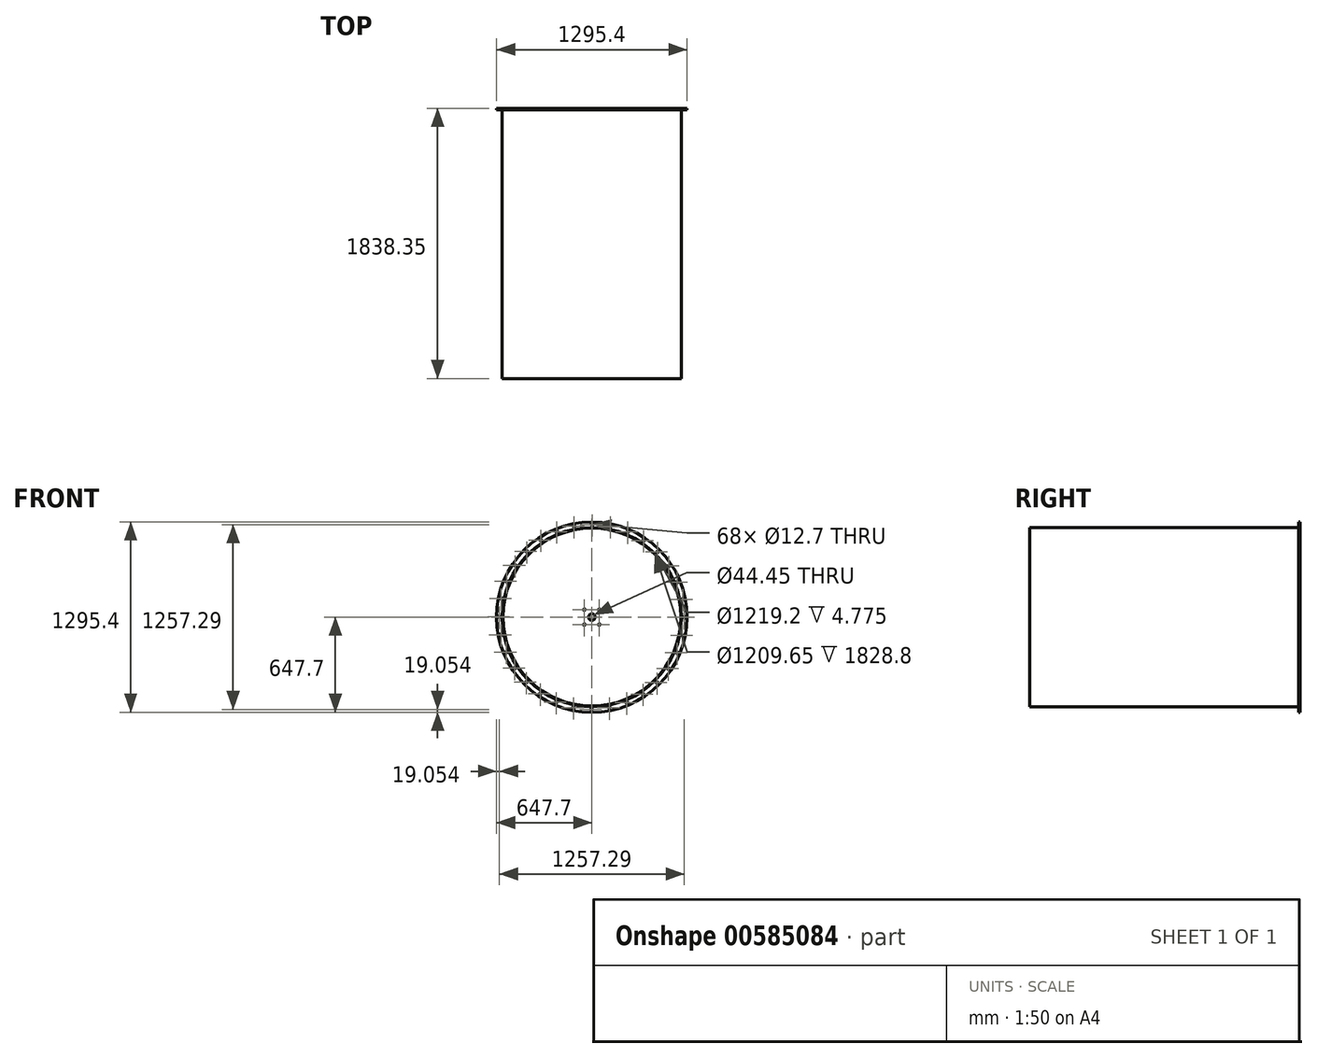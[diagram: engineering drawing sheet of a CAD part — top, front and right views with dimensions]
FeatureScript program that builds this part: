
annotation { "Feature Type Name" : "Feature", "Feature Type Description" : "" }
export const myFeature = defineFeature(function(context is Context, id is Id, definition is map)
    precondition{}
    {
        {
            var Q0;
            Q0=qCreatedBy(makeId("Front.planeOp"),FACE);
            var sketch = newSketch(context, id + "F0", { "sketchPlane" : qUnion([Q0])});
            skCircle(sketch, "E0", {"center": v(0, 0) * mm, "radius": 609.6 * mm});
            skCircle(sketch, "E1.0", {"center": v(0, 0) * mm, "radius": 604.82 * mm});
            skSolve(sketch);
        }
        {
            var Q0;
            Q0 = qSketchRegion(id + "F0", true);
            extrude(context, id + "F1", {"entities" : qUnion([Q0]), "depth" : 1828.8 * mm, "offsetDistance" : 25.4 * mm});
        }
        {
            var Q0;
            Q0=makeQuery(id+"F1.opExtrude","CAP_FACE",FACE,{"disambiguationData":[OSD([sQuery(id+"F0.wireOp",EDGE,"E0"),sQuery(id+"F0.wireOp",EDGE,"E1.0")])],"isStart":true});
            var sketch = newSketch(context, id + "F2", { "sketchPlane" : qUnion([Q0])});
            skCircle(sketch, "E2", {"center": v(0, 0) * mm, "radius": 609.6 * mm});
            skCircle(sketch, "E3", {"center": v(0, 0) * mm, "radius": 647.7 * mm});
            skCircle(sketch, "E4", {"center": v(-2.34, 628.65) * mm, "radius": 6.35 * mm});
            skCircle(sketch, "E5.1.0", {"center": v(-124.93, 616.11) * mm, "radius": 6.35 * mm});
            skCircle(sketch, "E5.2.0", {"center": v(-242.73, 579.9) * mm, "radius": 6.35 * mm});
            skCircle(sketch, "E5.3.0", {"center": v(-351.2, 521.4) * mm, "radius": 6.35 * mm});
            skCircle(sketch, "E5.4.0", {"center": v(-446.17, 442.87) * mm, "radius": 6.35 * mm});
            skCircle(sketch, "E5.5.0", {"center": v(-524, 347.31) * mm, "radius": 6.35 * mm});
            skCircle(sketch, "E5.6.0", {"center": v(-581.69, 238.41) * mm, "radius": 6.35 * mm});
            skCircle(sketch, "E5.7.0", {"center": v(-617.02, 120.35) * mm, "radius": 6.35 * mm});
            skCircle(sketch, "E5.8.0", {"center": v(-628.65, -2.34) * mm, "radius": 6.35 * mm});
            skCircle(sketch, "E5.9.0", {"center": v(-616.11, -124.93) * mm, "radius": 6.35 * mm});
            skCircle(sketch, "E5.10.0", {"center": v(-579.9, -242.73) * mm, "radius": 6.35 * mm});
            skCircle(sketch, "E5.11.0", {"center": v(-521.4, -351.2) * mm, "radius": 6.35 * mm});
            skCircle(sketch, "E5.12.0", {"center": v(-442.87, -446.17) * mm, "radius": 6.35 * mm});
            skCircle(sketch, "E5.13.0", {"center": v(-347.31, -524) * mm, "radius": 6.35 * mm});
            skCircle(sketch, "E5.14.0", {"center": v(-238.41, -581.69) * mm, "radius": 6.35 * mm});
            skCircle(sketch, "E5.15.0", {"center": v(-120.35, -617.02) * mm, "radius": 6.35 * mm});
            skCircle(sketch, "E6.1.16.0", {"center": v(2.34, -628.65) * mm, "radius": 6.35 * mm});
            skCircle(sketch, "E6.1.17.0", {"center": v(124.93, -616.11) * mm, "radius": 6.35 * mm});
            skCircle(sketch, "E6.1.18.0", {"center": v(242.73, -579.9) * mm, "radius": 6.35 * mm});
            skCircle(sketch, "E6.1.19.0", {"center": v(351.2, -521.4) * mm, "radius": 6.35 * mm});
            skCircle(sketch, "E7.1.20.0", {"center": v(446.17, -442.87) * mm, "radius": 6.35 * mm});
            skCircle(sketch, "E7.1.21.0", {"center": v(524, -347.31) * mm, "radius": 6.35 * mm});
            skCircle(sketch, "E7.1.22.0", {"center": v(581.69, -238.41) * mm, "radius": 6.35 * mm});
            skCircle(sketch, "E7.1.23.0", {"center": v(617.02, -120.35) * mm, "radius": 6.35 * mm});
            skCircle(sketch, "E7.1.24.0", {"center": v(628.65, 2.34) * mm, "radius": 6.35 * mm});
            skCircle(sketch, "E7.1.25.0", {"center": v(616.11, 124.93) * mm, "radius": 6.35 * mm});
            skCircle(sketch, "E8.1.26.0", {"center": v(579.9, 242.73) * mm, "radius": 6.35 * mm});
            skCircle(sketch, "E8.1.27.0", {"center": v(521.4, 351.2) * mm, "radius": 6.35 * mm});
            skCircle(sketch, "E8.1.28.0", {"center": v(442.87, 446.17) * mm, "radius": 6.35 * mm});
            skCircle(sketch, "E8.1.29.0", {"center": v(347.31, 524) * mm, "radius": 6.35 * mm});
            skCircle(sketch, "E8.1.30.0", {"center": v(238.41, 581.69) * mm, "radius": 6.35 * mm});
            skCircle(sketch, "E8.1.31.0", {"center": v(120.35, 617.02) * mm, "radius": 6.35 * mm});
            skSolve(sketch);
        }
        {
            var Q0;
            Q0 = qSketchRegion(id + "F2", true);
            extrude(context, id + "F3", {"entities" : qUnion([Q0]), "depth" : 4.78 * mm, "offsetDistance" : 25.4 * mm});
        }
        {
            var Q0;
            Q0=makeQuery(id+"F3.opExtrude","CAP_FACE",FACE,{"disambiguationData":[OSD([sQuery(id+"F2.wireOp",EDGE,"E2"),sQuery(id+"F2.wireOp",EDGE,"E3"),sQuery(id+"F2.wireOp",EDGE,"E4"),sQuery(id+"F2.wireOp",EDGE,"E5.1.0"),sQuery(id+"F2.wireOp",EDGE,"E5.2.0"),sQuery(id+"F2.wireOp",EDGE,"E5.3.0"),sQuery(id+"F2.wireOp",EDGE,"E5.4.0"),sQuery(id+"F2.wireOp",EDGE,"E5.5.0"),sQuery(id+"F2.wireOp",EDGE,"E5.6.0"),sQuery(id+"F2.wireOp",EDGE,"E5.7.0"),sQuery(id+"F2.wireOp",EDGE,"E5.8.0"),sQuery(id+"F2.wireOp",EDGE,"E5.9.0"),sQuery(id+"F2.wireOp",EDGE,"E5.10.0"),sQuery(id+"F2.wireOp",EDGE,"E5.11.0"),sQuery(id+"F2.wireOp",EDGE,"E5.12.0"),sQuery(id+"F2.wireOp",EDGE,"E5.13.0"),sQuery(id+"F2.wireOp",EDGE,"E5.14.0"),sQuery(id+"F2.wireOp",EDGE,"E5.15.0"),sQuery(id+"F2.wireOp",EDGE,"E6.1.16.0"),sQuery(id+"F2.wireOp",EDGE,"E6.1.17.0"),sQuery(id+"F2.wireOp",EDGE,"E6.1.18.0"),sQuery(id+"F2.wireOp",EDGE,"E6.1.19.0"),sQuery(id+"F2.wireOp",EDGE,"E7.1.20.0"),sQuery(id+"F2.wireOp",EDGE,"E7.1.21.0"),sQuery(id+"F2.wireOp",EDGE,"E7.1.22.0"),sQuery(id+"F2.wireOp",EDGE,"E7.1.23.0"),sQuery(id+"F2.wireOp",EDGE,"E7.1.24.0"),sQuery(id+"F2.wireOp",EDGE,"E7.1.25.0"),sQuery(id+"F2.wireOp",EDGE,"E8.1.26.0"),sQuery(id+"F2.wireOp",EDGE,"E8.1.27.0"),sQuery(id+"F2.wireOp",EDGE,"E8.1.28.0"),sQuery(id+"F2.wireOp",EDGE,"E8.1.29.0"),sQuery(id+"F2.wireOp",EDGE,"E8.1.30.0"),sQuery(id+"F2.wireOp",EDGE,"E8.1.31.0")])],"isStart":false});
            var sketch = newSketch(context, id + "F4", { "sketchPlane" : qUnion([Q0])});
            skCircle(sketch, "E9", {"center": v(0, 0) * mm, "radius": 647.7 * mm});
            skCircle(sketch, "E10", {"center": v(-2.34, 628.65) * mm, "radius": 6.35 * mm});
            skCircle(sketch, "E11.1.0", {"center": v(-124.93, 616.11) * mm, "radius": 6.35 * mm});
            skCircle(sketch, "E11.2.0", {"center": v(-242.73, 579.9) * mm, "radius": 6.35 * mm});
            skCircle(sketch, "E11.3.0", {"center": v(-351.2, 521.4) * mm, "radius": 6.35 * mm});
            skCircle(sketch, "E11.4.0", {"center": v(-446.17, 442.87) * mm, "radius": 6.35 * mm});
            skCircle(sketch, "E11.5.0", {"center": v(-524, 347.31) * mm, "radius": 6.35 * mm});
            skCircle(sketch, "E11.6.0", {"center": v(-581.69, 238.41) * mm, "radius": 6.35 * mm});
            skCircle(sketch, "E11.7.0", {"center": v(-617.02, 120.35) * mm, "radius": 6.35 * mm});
            skCircle(sketch, "E11.8.0", {"center": v(-628.65, -2.34) * mm, "radius": 6.35 * mm});
            skCircle(sketch, "E11.9.0", {"center": v(-616.11, -124.93) * mm, "radius": 6.35 * mm});
            skCircle(sketch, "E11.10.0", {"center": v(-579.9, -242.73) * mm, "radius": 6.35 * mm});
            skCircle(sketch, "E11.11.0", {"center": v(-521.4, -351.2) * mm, "radius": 6.35 * mm});
            skCircle(sketch, "E11.12.0", {"center": v(-442.87, -446.17) * mm, "radius": 6.35 * mm});
            skCircle(sketch, "E11.13.0", {"center": v(-347.31, -524) * mm, "radius": 6.35 * mm});
            skCircle(sketch, "E11.14.0", {"center": v(-238.41, -581.69) * mm, "radius": 6.35 * mm});
            skCircle(sketch, "E11.15.0", {"center": v(-120.35, -617.02) * mm, "radius": 6.35 * mm});
            skCircle(sketch, "E12.1.16.0", {"center": v(2.34, -628.65) * mm, "radius": 6.35 * mm});
            skCircle(sketch, "E12.1.17.0", {"center": v(124.93, -616.11) * mm, "radius": 6.35 * mm});
            skCircle(sketch, "E12.1.18.0", {"center": v(242.73, -579.9) * mm, "radius": 6.35 * mm});
            skCircle(sketch, "E12.1.19.0", {"center": v(351.2, -521.4) * mm, "radius": 6.35 * mm});
            skCircle(sketch, "E13.1.20.0", {"center": v(446.17, -442.87) * mm, "radius": 6.35 * mm});
            skCircle(sketch, "E13.1.21.0", {"center": v(524, -347.31) * mm, "radius": 6.35 * mm});
            skCircle(sketch, "E13.1.22.0", {"center": v(581.69, -238.41) * mm, "radius": 6.35 * mm});
            skCircle(sketch, "E13.1.23.0", {"center": v(617.02, -120.35) * mm, "radius": 6.35 * mm});
            skCircle(sketch, "E13.1.24.0", {"center": v(628.65, 2.34) * mm, "radius": 6.35 * mm});
            skCircle(sketch, "E13.1.25.0", {"center": v(616.11, 124.93) * mm, "radius": 6.35 * mm});
            skCircle(sketch, "E14.1.26.0", {"center": v(579.9, 242.73) * mm, "radius": 6.35 * mm});
            skCircle(sketch, "E14.1.27.0", {"center": v(521.4, 351.2) * mm, "radius": 6.35 * mm});
            skCircle(sketch, "E14.1.28.0", {"center": v(442.87, 446.17) * mm, "radius": 6.35 * mm});
            skCircle(sketch, "E14.1.29.0", {"center": v(347.31, 524) * mm, "radius": 6.35 * mm});
            skCircle(sketch, "E14.1.30.0", {"center": v(238.41, 581.69) * mm, "radius": 6.35 * mm});
            skCircle(sketch, "E14.1.31.0", {"center": v(120.35, 617.02) * mm, "radius": 6.35 * mm});
            skSolve(sketch);
        }
        {
            var Q0;
            Q0 = qSketchRegion(id + "F4", true);
            extrude(context, id + "F5", {"entities" : qUnion([Q0]), "depth" : 4.78 * mm, "offsetDistance" : 25.4 * mm});
        }
        {
            var Q0;
            Q0=makeQuery(id+"F5.opExtrude","CAP_FACE",FACE,{"disambiguationData":[OSD([sQuery(id+"F4.wireOp",EDGE,"E9"),sQuery(id+"F4.wireOp",EDGE,"E10"),sQuery(id+"F4.wireOp",EDGE,"E11.1.0"),sQuery(id+"F4.wireOp",EDGE,"E11.2.0"),sQuery(id+"F4.wireOp",EDGE,"E11.3.0"),sQuery(id+"F4.wireOp",EDGE,"E11.4.0"),sQuery(id+"F4.wireOp",EDGE,"E11.5.0"),sQuery(id+"F4.wireOp",EDGE,"E11.6.0"),sQuery(id+"F4.wireOp",EDGE,"E11.7.0"),sQuery(id+"F4.wireOp",EDGE,"E11.8.0"),sQuery(id+"F4.wireOp",EDGE,"E11.9.0"),sQuery(id+"F4.wireOp",EDGE,"E11.10.0"),sQuery(id+"F4.wireOp",EDGE,"E11.11.0"),sQuery(id+"F4.wireOp",EDGE,"E11.12.0"),sQuery(id+"F4.wireOp",EDGE,"E11.13.0"),sQuery(id+"F4.wireOp",EDGE,"E11.14.0"),sQuery(id+"F4.wireOp",EDGE,"E11.15.0"),sQuery(id+"F4.wireOp",EDGE,"E12.1.16.0"),sQuery(id+"F4.wireOp",EDGE,"E12.1.17.0"),sQuery(id+"F4.wireOp",EDGE,"E12.1.18.0"),sQuery(id+"F4.wireOp",EDGE,"E12.1.19.0"),sQuery(id+"F4.wireOp",EDGE,"E13.1.20.0"),sQuery(id+"F4.wireOp",EDGE,"E13.1.21.0"),sQuery(id+"F4.wireOp",EDGE,"E13.1.22.0"),sQuery(id+"F4.wireOp",EDGE,"E13.1.23.0"),sQuery(id+"F4.wireOp",EDGE,"E13.1.24.0"),sQuery(id+"F4.wireOp",EDGE,"E13.1.25.0"),sQuery(id+"F4.wireOp",EDGE,"E14.1.26.0"),sQuery(id+"F4.wireOp",EDGE,"E14.1.27.0"),sQuery(id+"F4.wireOp",EDGE,"E14.1.28.0"),sQuery(id+"F4.wireOp",EDGE,"E14.1.29.0"),sQuery(id+"F4.wireOp",EDGE,"E14.1.30.0"),sQuery(id+"F4.wireOp",EDGE,"E14.1.31.0")])],"isStart":false});
            var sketch = newSketch(context, id + "F6", { "sketchPlane" : qUnion([Q0])});
            skCircle(sketch, "E15", {"center": v(0, 0) * mm, "radius": 22.23 * mm});
            skLineSegment(sketch, "E16.bottom", {"start": v(50.8, 50.8) * mm, "end": v(-50.8, 50.8) * mm, "construction": true});
            skLineSegment(sketch, "E16.top", {"start": v(50.8, -50.8) * mm, "end": v(-50.8, -50.8) * mm, "construction": true});
            skLineSegment(sketch, "E16.left", {"start": v(50.8, 50.8) * mm, "end": v(50.8, -50.8) * mm, "construction": true});
            skLineSegment(sketch, "E16.right", {"start": v(-50.8, 50.8) * mm, "end": v(-50.8, -50.8) * mm, "construction": true});
            skCircle(sketch, "E17", {"center": v(50.8, 50.8) * mm, "radius": 6.35 * mm});
            skCircle(sketch, "E18.1.0", {"center": v(-50.8, 50.8) * mm, "radius": 6.35 * mm});
            skCircle(sketch, "E18.2.0", {"center": v(-50.8, -50.8) * mm, "radius": 6.35 * mm});
            skCircle(sketch, "E18.3.0", {"center": v(50.8, -50.8) * mm, "radius": 6.35 * mm});
            skSolve(sketch);
        }
        {
            var Q0;
            Q0 = qSketchRegion(id + "F6", true);
            extrude(context, id + "F7", {"entities" : qUnion([Q0]), "operationType" : NewBodyOperationType.REMOVE, "oppositeDirection" : true, "depth" : 25.4 * mm, "offsetDistance" : 25.4 * mm});
        }
    });
